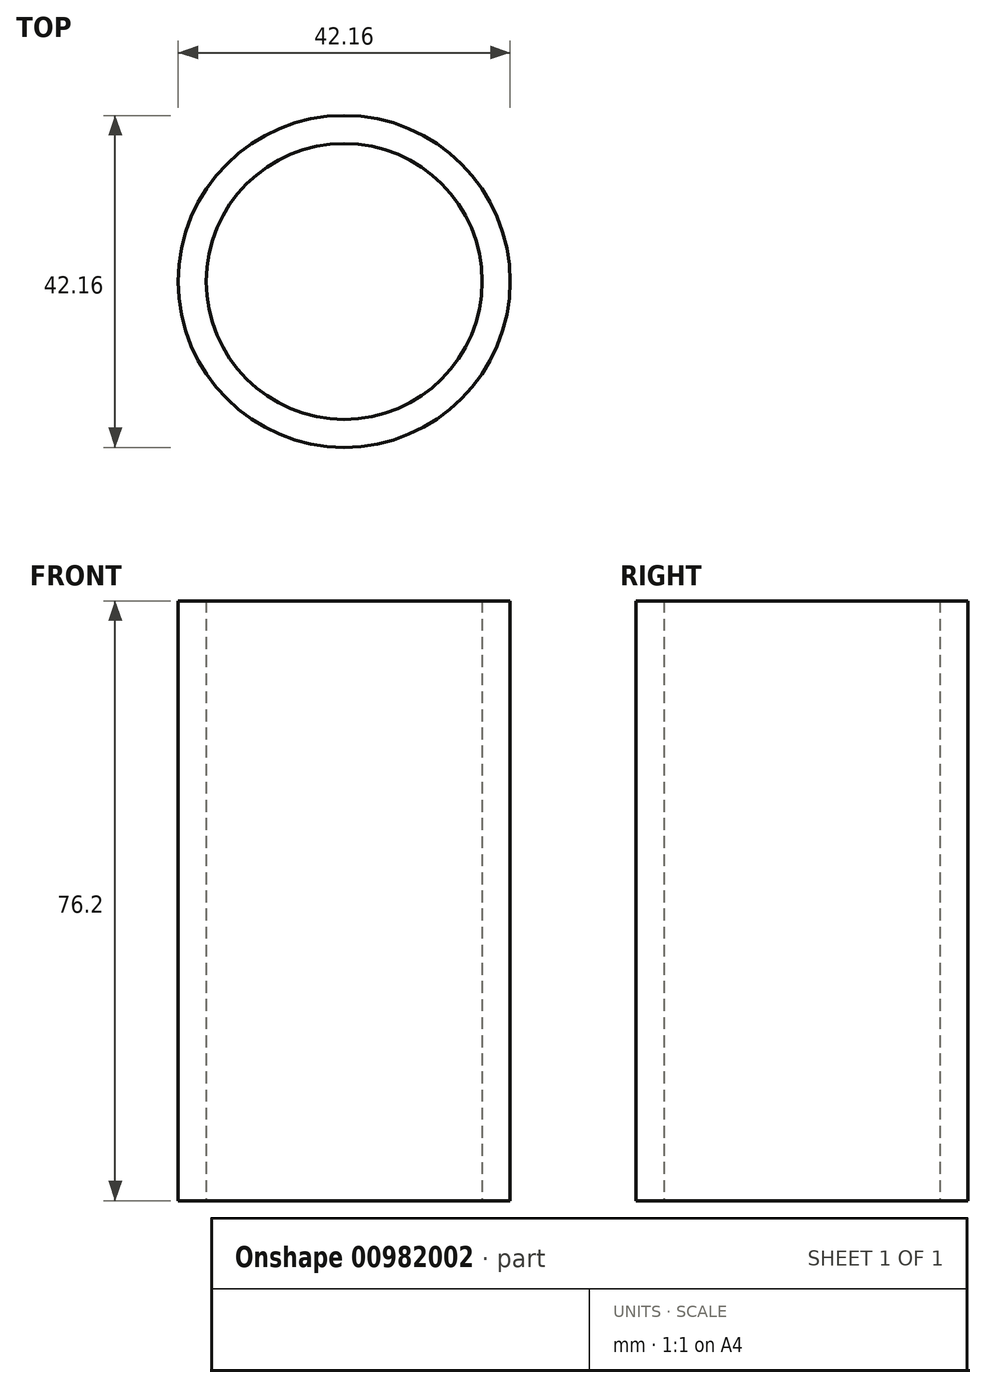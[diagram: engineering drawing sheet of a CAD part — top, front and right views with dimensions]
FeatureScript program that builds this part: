
annotation { "Feature Type Name" : "Feature", "Feature Type Description" : "" }
export const myFeature = defineFeature(function(context is Context, id is Id, definition is map)
    precondition{}
    {
        {
            var Q0;
            Q0=qCreatedBy(makeId("Top.planeOp"),FACE);
            var sketch = newSketch(context, id + "F0", { "sketchPlane" : qUnion([Q0])});
            skCircle(sketch, "E0", {"center": v(0, 0) * mm, "radius": 17.53 * mm});
            skCircle(sketch, "E1", {"center": v(0, 0) * mm, "radius": 21.08 * mm});
            skSolve(sketch);
        }
        {
            var Q0;
            Q0=qSketchRegion(id+"F0",true);
            extrude(context, id + "F1", {"entities" : qUnion([Q0]), "depth" : 76.2 * mm, "offsetDistance" : 25.4 * mm});
        }
    });
